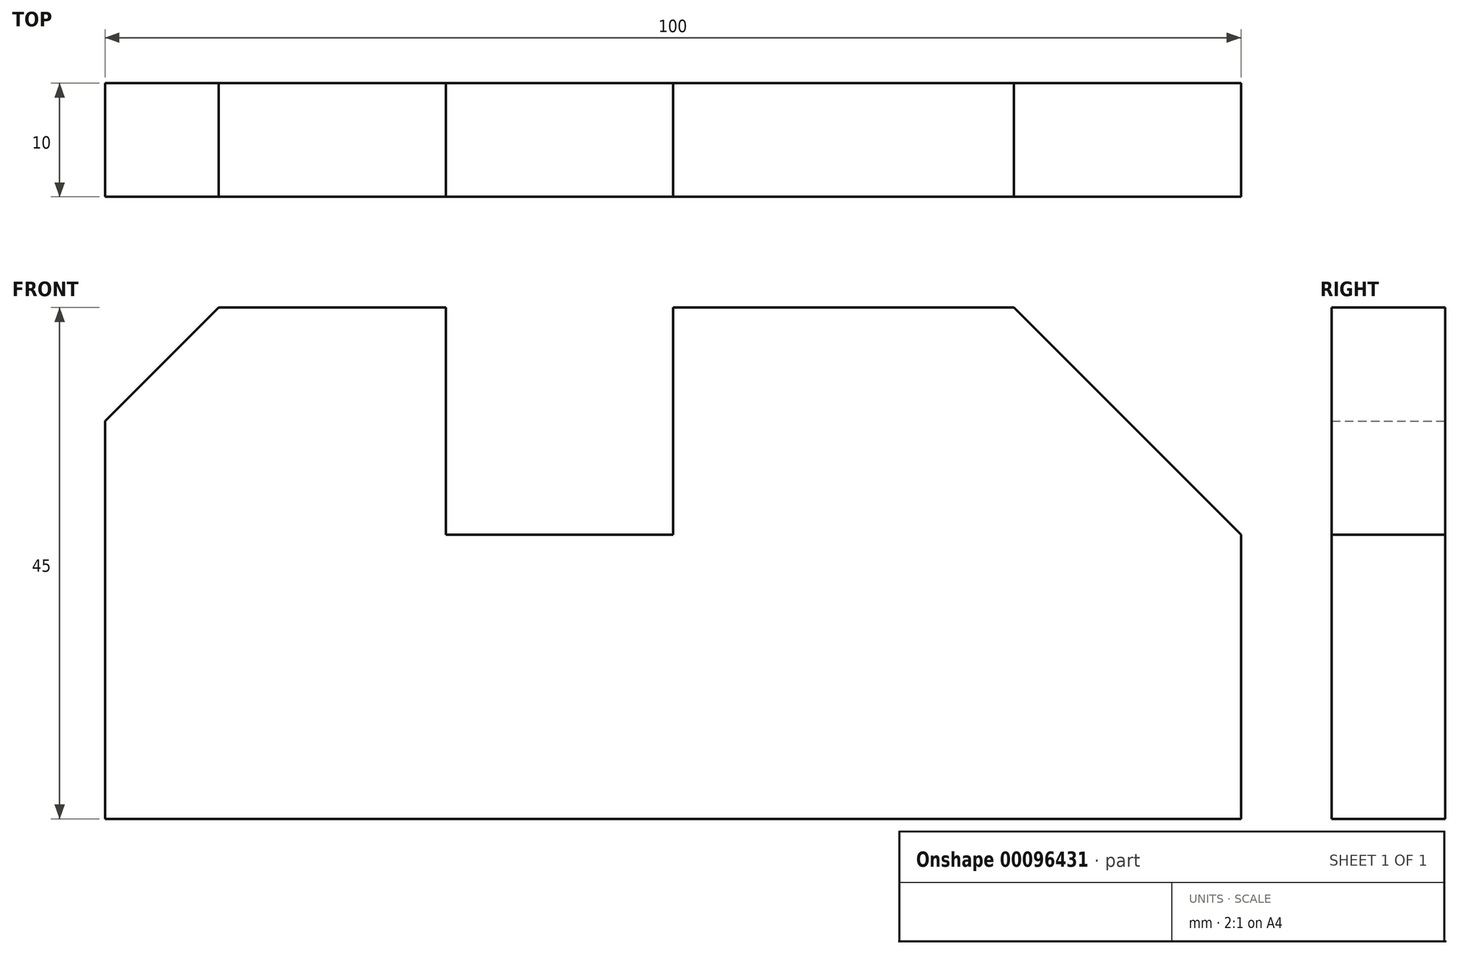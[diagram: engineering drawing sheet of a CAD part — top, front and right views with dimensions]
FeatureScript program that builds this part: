
annotation { "Feature Type Name" : "Feature", "Feature Type Description" : "" }
export const myFeature = defineFeature(function(context is Context, id is Id, definition is map)
    precondition{}
    {
        {
            var Q0;
            Q0=qCreatedBy(makeId("Front.planeOp"),FACE);
            var sketch = newSketch(context, id + "F0", { "sketchPlane" : qUnion([Q0])});
            skLineSegment(sketch, "E0", {"start": v(0, 0) * mm, "end": v(0, 35) * mm});
            skLineSegment(sketch, "E1", {"start": v(0, 35) * mm, "end": v(10, 45) * mm});
            skLineSegment(sketch, "E2", {"start": v(10, 45) * mm, "end": v(30, 45) * mm});
            skLineSegment(sketch, "E3", {"start": v(30, 45) * mm, "end": v(30, 25) * mm});
            skLineSegment(sketch, "E4", {"start": v(30, 25) * mm, "end": v(50, 25) * mm});
            skLineSegment(sketch, "E5", {"start": v(50, 25) * mm, "end": v(50, 45) * mm});
            skLineSegment(sketch, "E6", {"start": v(50, 45) * mm, "end": v(80, 45) * mm});
            skLineSegment(sketch, "E7", {"start": v(80, 45) * mm, "end": v(100, 25) * mm});
            skLineSegment(sketch, "E8", {"start": v(100, 25) * mm, "end": v(100, 0) * mm});
            skLineSegment(sketch, "E9", {"start": v(100, 0) * mm, "end": v(0, 0) * mm});
            skSolve(sketch);
        }
        {
            var Q0;
            Q0=makeQuery(id+"F0.imprint","IMPRINT",FACE,{"disambiguationData":[TD([[makeQuery(id+"F0.imprint","IMPRINT",EDGE,{"derivedFrom":sQuery(id+"F0.wireOp",EDGE,"E0")}),-1.0]])]});
            extrude(context, id + "F1", {"entities" : qUnion([Q0]), "depth" : 10 * mm});
        }
    });
